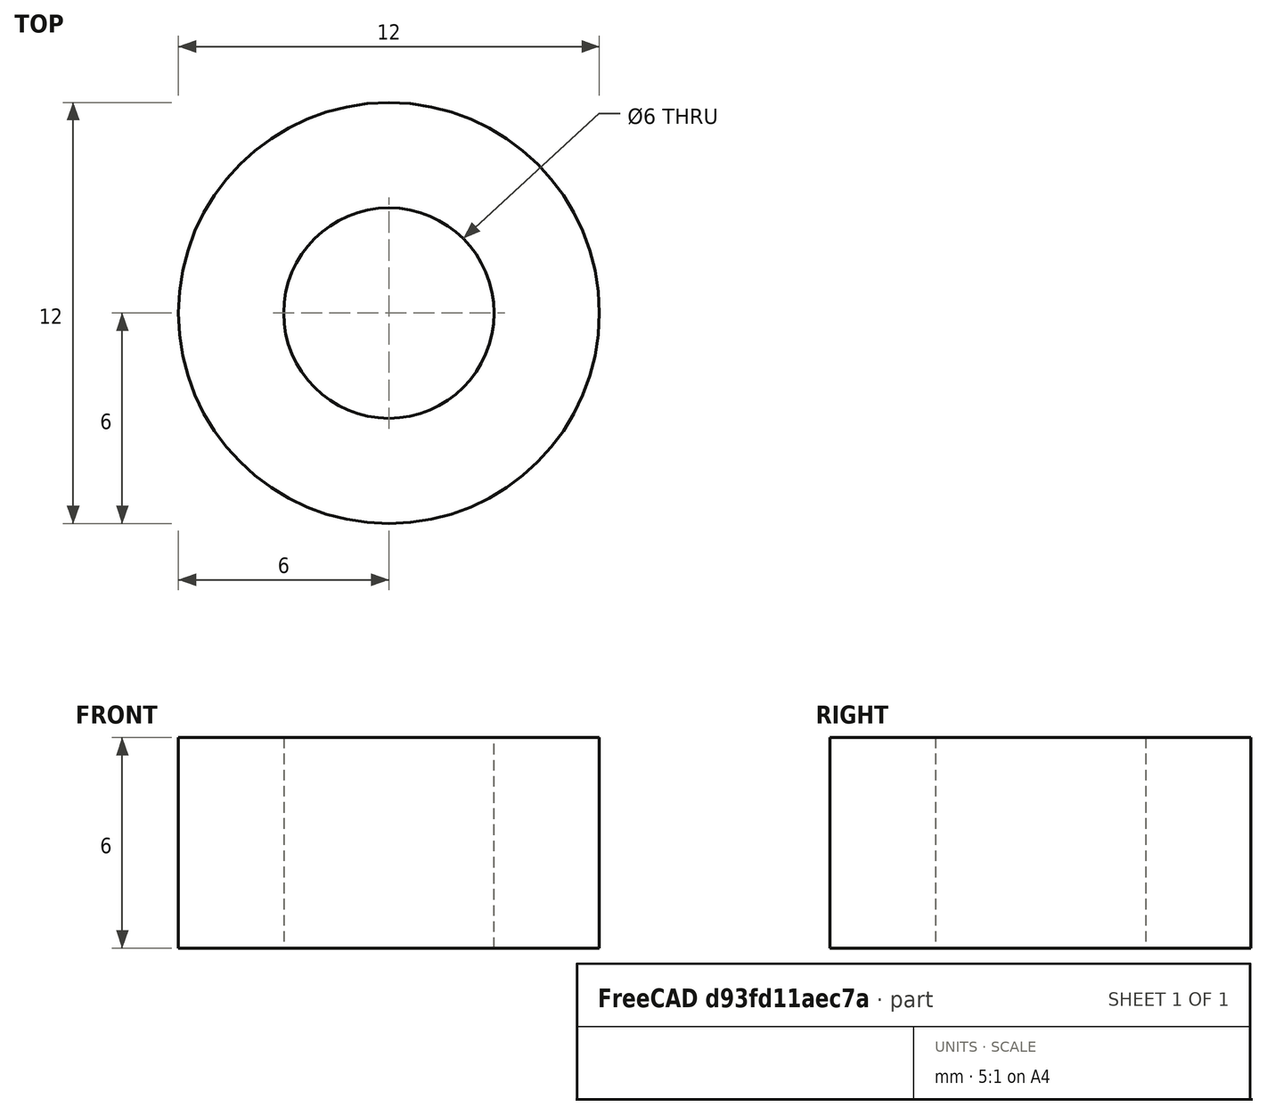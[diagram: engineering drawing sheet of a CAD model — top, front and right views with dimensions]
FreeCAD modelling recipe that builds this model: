
FCSTD DOCUMENT  (FreeCAD 0.17R8073 (Git))
Label: 6mm_M5_thumbscrew_spacer
License: CreativeCommons Attribution-ShareAlike
LicenseURL: http://creativecommons.org/licenses/by-sa/4.0/
objects: Sketcher::SketchObject×1, PartDesign::Pad×1, PartDesign::Body×1
note: 4 computed .brp shape members not serialized (recipe doc carries the construction recipe); baked Part::Feature solids carry a one-line shape summary decoded from their .brp

FEATURE [Sketcher::SketchObject] Sketch
  MapMode = 5
  Support = -> [XY_Plane]
  sketch-geometry (2):
    g0: Circle CenterX=0 CenterY=0 CenterZ=0 NormalX=0 NormalY=0 NormalZ=1 Radius=6
    g1: Circle CenterX=0 CenterY=0 CenterZ=0 NormalX=0 NormalY=0 NormalZ=1 Radius=3
  constraints (4):
    c: Coincident(g0,g-1)
    c: Radius(g0) = 6
    c: Coincident(g0,g1)
    c: Radius(g1) = 3
FEATURE [PartDesign::Pad] Pad
  Length = 6
  Length2 = 100
  Profile = -> Sketch
  Type = 0
FEATURE [PartDesign::Body] Body
  Model = -> [Sketch,Pad]
  Origin = -> BodyOrigin
  Tip = -> Pad
